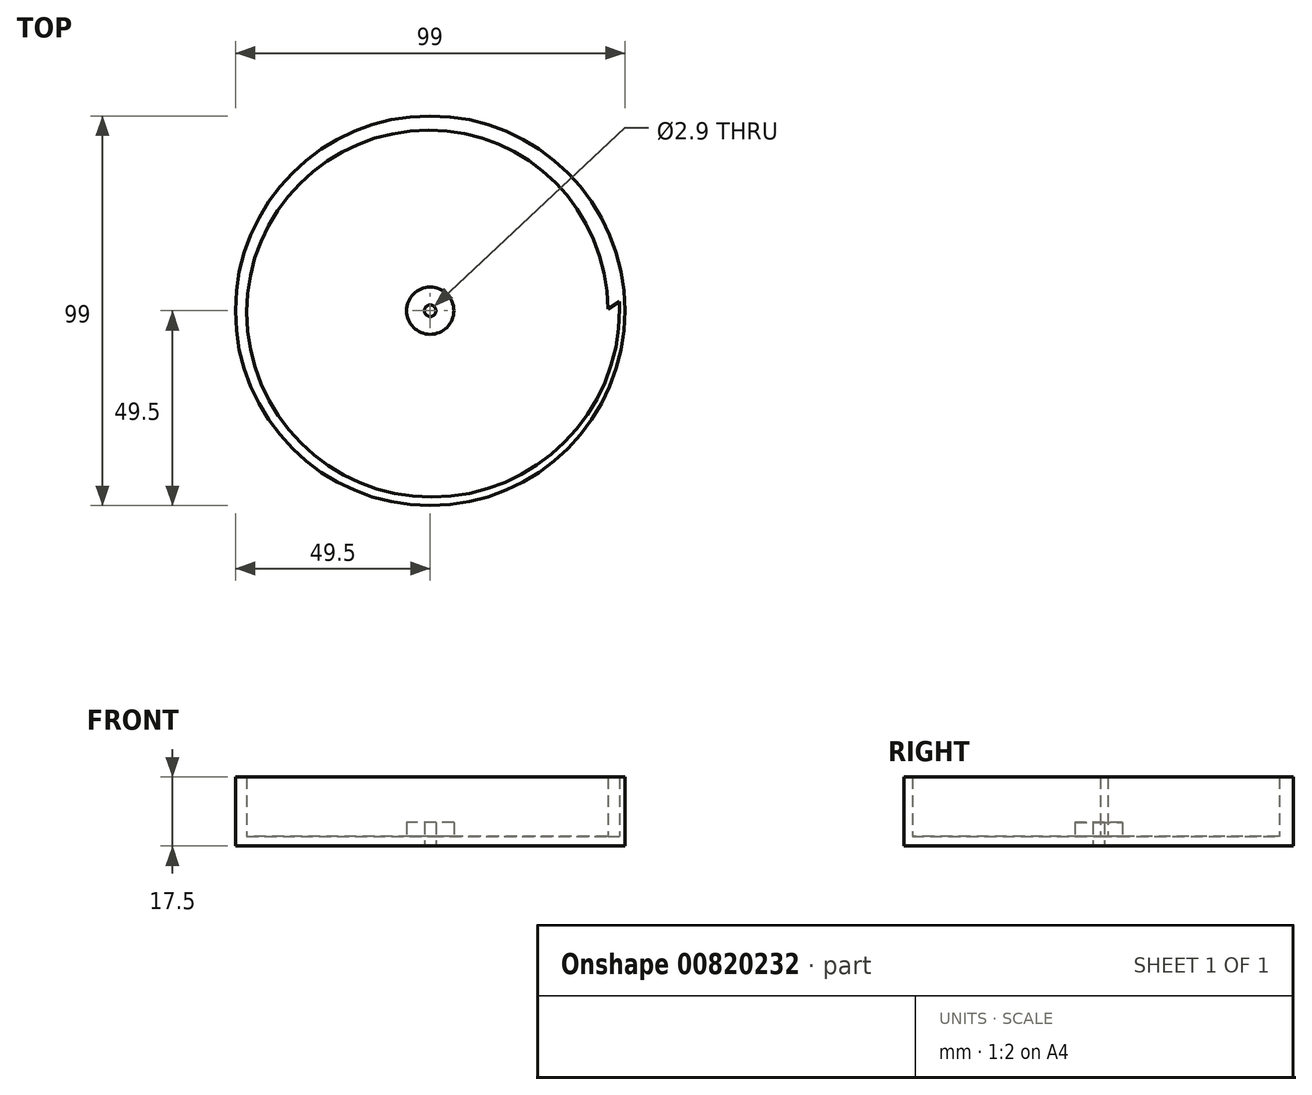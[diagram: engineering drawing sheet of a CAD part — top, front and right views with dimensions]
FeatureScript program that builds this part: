
annotation { "Feature Type Name" : "Feature", "Feature Type Description" : "" }
export const myFeature = defineFeature(function(context is Context, id is Id, definition is map)
    precondition{}
    {
        {
            var Q0;
            Q0=qCreatedBy(makeId("Top.planeOp"),FACE);
            var sketch = newSketch(context, id + "F0", { "sketchPlane" : qUnion([Q0])});
            skCircle(sketch, "E0", {"center": v(0, 0) * mm, "radius": 49.5 * mm});
            skCircle(sketch, "E1", {"center": v(0, 0) * mm, "radius": 1.45 * mm});
            skSolve(sketch);
        }
        {
            var Q0;
            Q0=makeQuery(id+"F0.imprint","IMPRINT",FACE,{"disambiguationData":[TD([[makeQuery(id+"F0.imprint","IMPRINT",EDGE,{"derivedFrom":sQuery(id+"F0.wireOp",EDGE,"E0")}),1.0]])]});
            extrude(context, id + "F1", {"entities" : qUnion([Q0]), "depth" : 2.5 * mm, "offsetDistance" : 25 * mm});
        }
        {
            var Q0;
            Q0=makeQuery(id+"F1.opExtrude","CAP_FACE",FACE,{"disambiguationData":[OSD([sQuery(id+"F0.wireOp",EDGE,"E0"),sQuery(id+"F0.wireOp",EDGE,"E1")])],"isStart":false});
            var sketch = newSketch(context, id + "F2", { "sketchPlane" : qUnion([Q0])});
            skCircle(sketch, "E2", {"center": v(0, 0) * mm, "radius": 6 * mm});
            skSolve(sketch);
        }
        {
            var Q0;
            Q0=makeQuery(id+"F2.imprint","IMPRINT",FACE,{"disambiguationData":[TD([[makeQuery(id+"F2.imprint","IMPRINT",EDGE,{"derivedFrom":sQuery(id+"F2.wireOp",EDGE,"E2")}),1.0]])]});
            extrude(context, id + "F3", {"entities" : qUnion([Q0]), "operationType" : NewBodyOperationType.ADD, "depth" : 3.5 * mm, "offsetDistance" : 25 * mm});
        }
        {
            var Q0;
            Q0=makeQuery(id+"F1.opExtrude","CAP_FACE",FACE,{"disambiguationData":[OSD([sQuery(id+"F0.wireOp",EDGE,"E0"),sQuery(id+"F0.wireOp",EDGE,"E1")])],"isStart":false});
            var sketch = newSketch(context, id + "F4", { "sketchPlane" : qUnion([Q0])});
            skLineSegment(sketch, "E3.bottom", {"start": v(0.37, 0.38) * mm, "end": v(-0.38, 0.38) * mm});
            skLineSegment(sketch, "E3.top", {"start": v(0.38, -0.38) * mm, "end": v(-0.37, -0.38) * mm});
            skLineSegment(sketch, "E3.left", {"start": v(0.37, 0.38) * mm, "end": v(0.37, -0.38) * mm});
            skLineSegment(sketch, "E3.right", {"start": v(-0.37, 0.38) * mm, "end": v(-0.37, -0.38) * mm});
            skPoint(sketch, "E3.middle", {"position": v(0, 0) * mm});
            skLineSegment(sketch, "E4", {"start": v(0.37, 0.38) * mm, "end": v(45.12, 0.38) * mm, "construction": true});
            skLineSegment(sketch, "E5", {"start": v(-0.38, 0.38) * mm, "end": v(-0.38, 49.6) * mm, "construction": true});
            skLineSegment(sketch, "E6", {"start": v(-0.37, -0.38) * mm, "end": v(-58.1, -0.38) * mm, "construction": true});
            skLineSegment(sketch, "E7", {"start": v(0.38, -0.38) * mm, "end": v(0.38, -59.06) * mm, "construction": true});
            skArc(sketch, "E8", {"start": v(45.12, 0.38) * mm, "mid": v(31.8, 32.55) * mm, "end": v(-0.38, 45.88) * mm});
            skArc(sketch, "E9", {"start": v(-0.38, 45.88) * mm, "mid": v(-33.08, 32.33) * mm, "end": v(-46.62, -0.38) * mm});
            skArc(sketch, "E10", {"start": v(-46.62, -0.38) * mm, "mid": v(-32.86, -33.6) * mm, "end": v(0.38, -47.38) * mm});
            skArc(sketch, "E11", {"start": v(0.38, -47.38) * mm, "mid": v(34.14, -33.39) * mm, "end": v(48.12, 0.38) * mm});
            skLineSegment(sketch, "E12", {"start": v(45.12, 0.38) * mm, "end": v(69.13, 0.38) * mm, "construction": true});
            skArc(sketch, "E13", {"start": v(48.12, 0.38) * mm, "mid": v(48.1, 1.38) * mm, "end": v(48.07, 2.38) * mm});
            skLineSegment(sketch, "E14", {"start": v(45.12, 0.38) * mm, "end": v(48.07, 2.38) * mm});
            skCircle(sketch, "E15", {"center": v(0, 0) * mm, "radius": 49.5 * mm});
            skSolve(sketch);
        }
        {
            var Q0;
            Q0=makeQuery(id+"F4.imprint","IMPRINT",FACE,{"disambiguationData":[TD([[makeQuery(id+"F4.imprint","IMPRINT",EDGE,{"derivedFrom":sQuery(id+"F4.wireOp",EDGE,"E8")}),-1.0]])]});
            extrude(context, id + "F5", {"entities" : qUnion([Q0]), "operationType" : NewBodyOperationType.ADD, "depth" : 15 * mm, "offsetDistance" : 25 * mm});
        }
    });
